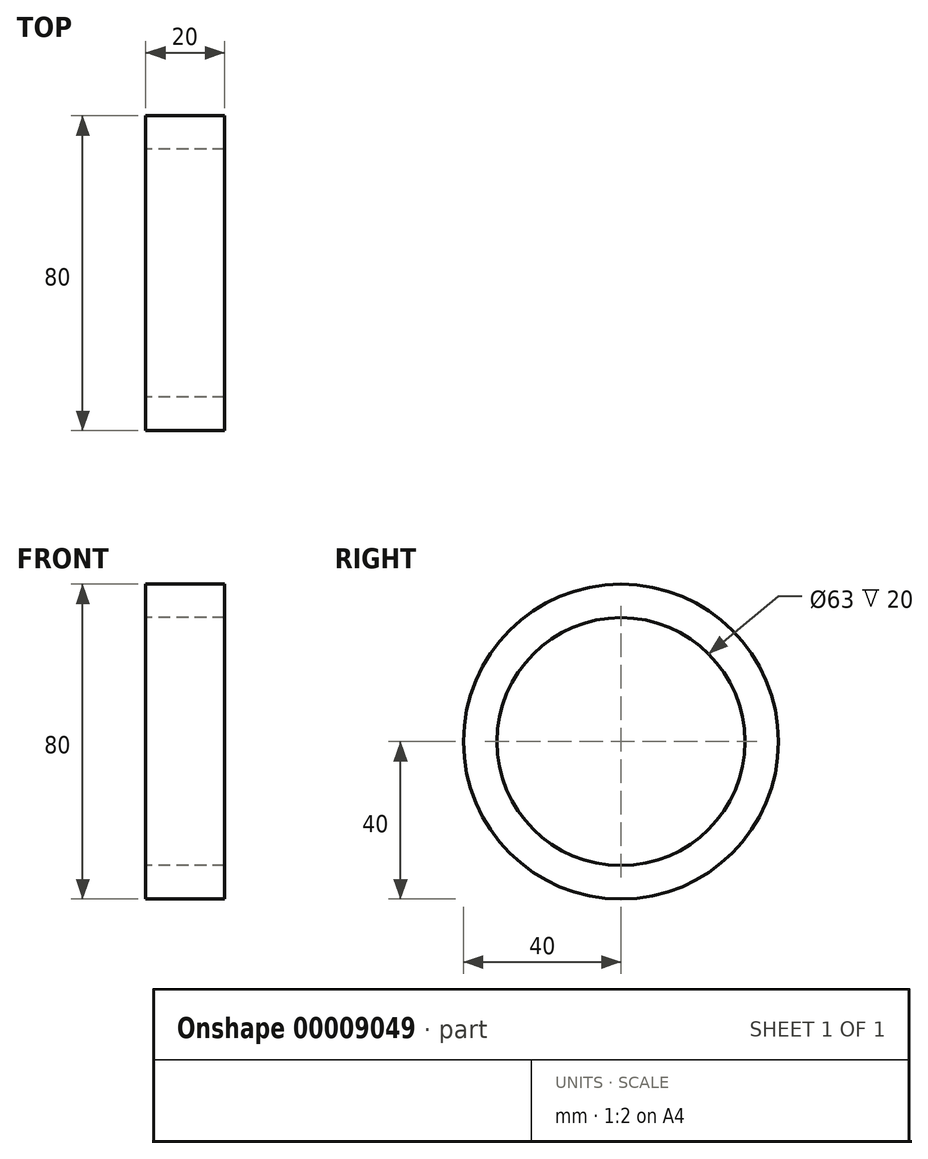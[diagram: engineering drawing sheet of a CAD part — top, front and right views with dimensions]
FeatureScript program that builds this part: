
annotation { "Feature Type Name" : "Feature", "Feature Type Description" : "" }
export const myFeature = defineFeature(function(context is Context, id is Id, definition is map)
    precondition{}
    {
        {
            var Q0;
            Q0=qCreatedBy(makeId("Right.planeOp"),FACE);
            var sketch = newSketch(context, id + "F0", { "sketchPlane" : qUnion([Q0])});
            skCircle(sketch, "E0", {"center": v(0, 0) * mm, "radius": 31.5 * mm});
            skCircle(sketch, "E1", {"center": v(0, 0) * mm, "radius": 40 * mm});
            skSolve(sketch);
        }
        {
            var Q0;
            Q0 = qSketchRegion(id + "F0", true);
            extrude(context, id + "F1", {"entities" : qUnion([Q0]), "depth" : 20 * mm});
        }
    });
